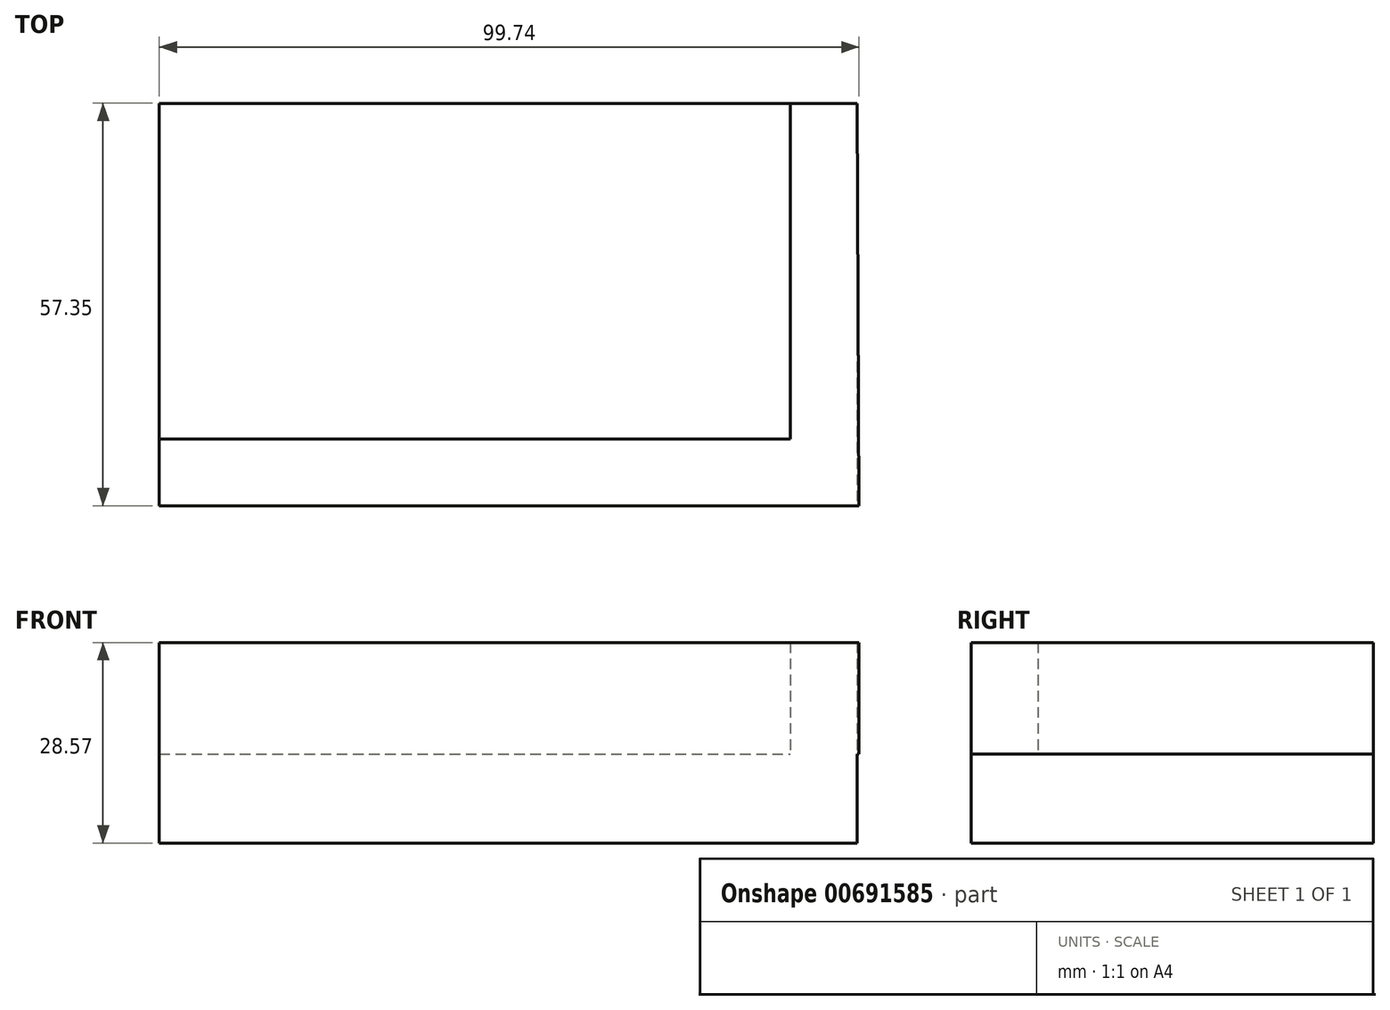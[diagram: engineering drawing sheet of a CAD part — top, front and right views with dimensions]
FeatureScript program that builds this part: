
annotation { "Feature Type Name" : "Feature", "Feature Type Description" : "" }
export const myFeature = defineFeature(function(context is Context, id is Id, definition is map)
    precondition{}
    {
        {
            var Q0;
            Q0=qCreatedBy(makeId("Top.planeOp"),FACE);
            var sketch = newSketch(context, id + "F0", { "sketchPlane" : qUnion([Q0])});
            skLineSegment(sketch, "E0.bottom", {"start": v(-49.87, 28.92) * mm, "end": v(49.62, 28.92) * mm});
            skLineSegment(sketch, "E0.top", {"start": v(-49.87, -28.43) * mm, "end": v(49.62, -28.43) * mm});
            skLineSegment(sketch, "E0.left", {"start": v(-49.87, 28.92) * mm, "end": v(-49.87, -28.43) * mm});
            skLineSegment(sketch, "E0.right", {"start": v(49.62, 28.92) * mm, "end": v(49.62, -28.43) * mm});
            skSolve(sketch);
        }
        {
            var Q0;
            Q0 = qSketchRegion(id + "F0", true);
            extrude(context, id + "F1", {"entities" : qUnion([Q0]), "depth" : 12.7 * mm, "offsetDistance" : 25.4 * mm});
        }
        {
            var Q0;
            Q0=makeQuery(id+"F1.opExtrude","CAP_FACE",FACE,{"disambiguationData":[OSD([sQuery(id+"F0.wireOp",EDGE,"E0.bottom"),sQuery(id+"F0.wireOp",EDGE,"E0.top"),sQuery(id+"F0.wireOp",EDGE,"E0.left"),sQuery(id+"F0.wireOp",EDGE,"E0.right")])],"isStart":false});
            var sketch = newSketch(context, id + "F2", { "sketchPlane" : qUnion([Q0])});
            skLineSegment(sketch, "E1.bottom", {"start": v(49.62, 28.92) * mm, "end": v(40.1, 28.92) * mm});
            skLineSegment(sketch, "E1.top", {"start": v(49.62, -28.43) * mm, "end": v(40.1, -28.43) * mm});
            skLineSegment(sketch, "E1.right", {"start": v(40.1, 28.92) * mm, "end": v(40.1, -18.9) * mm});
            skLineSegment(sketch, "E2.bottom", {"start": v(-49.87, -28.43) * mm, "end": v(49.87, -28.43) * mm});
            skLineSegment(sketch, "E2.top", {"start": v(-49.87, -18.9) * mm, "end": v(40.1, -18.9) * mm});
            skLineSegment(sketch, "E2.left", {"start": v(-49.87, -28.43) * mm, "end": v(-49.87, -18.9) * mm});
            skLineSegment(sketch, "E3.trimOffspring", {"start": v(49.62, -18.9) * mm, "end": v(49.87, -18.9) * mm});
            skLineSegment(sketch, "E4", {"start": v(49.62, 28.92) * mm, "end": v(49.87, -28.43) * mm});
            skSolve(sketch);
        }
        {
            var Q0;
            Q0 = qSketchRegion(id + "F2", true);
            extrude(context, id + "F3", {"entities" : qUnion([Q0]), "operationType" : NewBodyOperationType.ADD, "depth" : 15.88 * mm, "offsetDistance" : 25.4 * mm});
        }
    });
